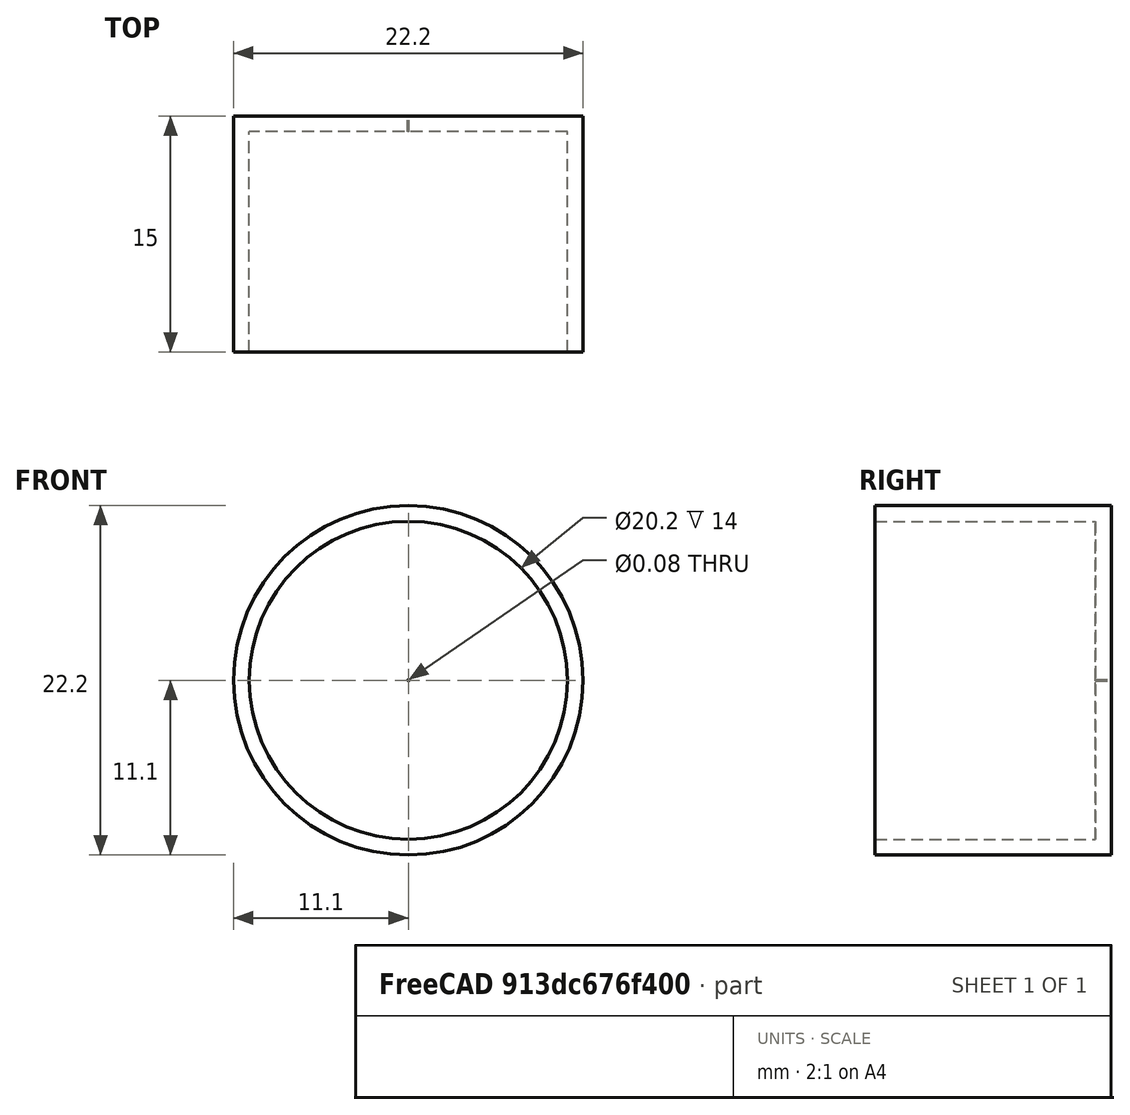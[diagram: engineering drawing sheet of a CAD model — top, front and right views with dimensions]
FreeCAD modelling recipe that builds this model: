
FCSTD DOCUMENT  (FreeCAD 0.18R16117 (Git))
Label: jeu poisson support 1
License: All rights reserved
LicenseURL: http://en.wikipedia.org/wiki/All_rights_reserved
objects: Sketcher::SketchObject×1, PartDesign::Revolution×1, PartDesign::Body×1
note: 4 computed .brp shape members not serialized (recipe doc carries the construction recipe); baked Part::Feature solids carry a one-line shape summary decoded from their .brp

FEATURE [Sketcher::SketchObject] Sketch
  MapMode = 5
  Support = -> [XY_Plane]
  sketch-geometry (6):
    g0: LineSegment StartX=10.1 StartY=-8.28261 StartZ=0 EndX=10.1 EndY=5.71739 EndZ=0
    g1: LineSegment StartX=10.1 StartY=5.71739 StartZ=0 EndX=0.041586 EndY=5.71739 EndZ=0
    g2: LineSegment StartX=0.041586 StartY=5.71739 StartZ=0 EndX=0.041586 EndY=6.71739 EndZ=0
    g3: LineSegment StartX=0.041586 StartY=6.71739 StartZ=0 EndX=11.1 EndY=6.71739 EndZ=0
    g4: LineSegment StartX=11.1 StartY=6.71739 StartZ=0 EndX=11.1 EndY=-8.28261 EndZ=0
    g5: LineSegment StartX=11.1 StartY=-8.28261 StartZ=0 EndX=10.1 EndY=-8.28261 EndZ=0
  constraints (16):
    c: Coincident(g0,g1)
    c: Coincident(g1,g2)
    c: Coincident(g2,g3)
    c: Coincident(g3,g4)
    c: Coincident(g4,g5)
    c: Coincident(g5,g0)
    c: DistanceX(g-2,g0) = 10.1
    c: Vertical(g0)
    c: Horizontal(g5)
    c: Horizontal(g3)
    c: Vertical(g4)
    c: Vertical(g2)
    c: DistanceX(g5,g5) = 1
    c: DistanceY(g0,g0) = 14
    c: Horizontal(g1)
    c: DistanceY(g2,g2) = 1
FEATURE [PartDesign::Revolution] Revolution
  Angle = 360
  Axis = (0,1,0)
  Base = (0,0,0)
  Profile = -> Sketch
  ReferenceAxis = -> Sketch [V_Axis]
  Reversed = true
FEATURE [PartDesign::Body] Body
  Group = -> [Sketch,Revolution]
  Origin = -> Origin
  Tip = -> Revolution
